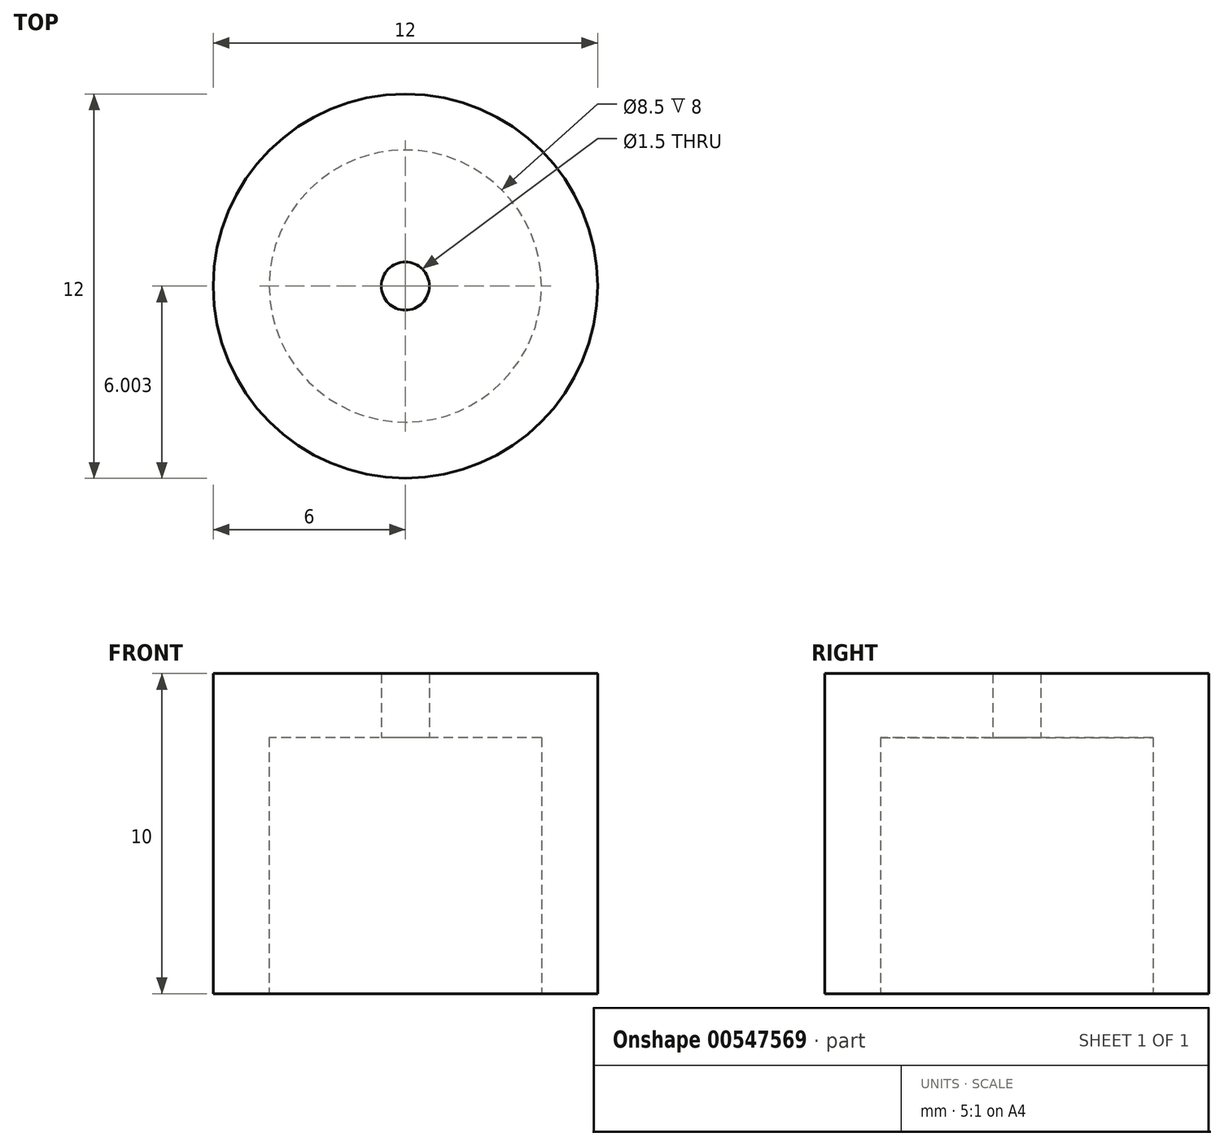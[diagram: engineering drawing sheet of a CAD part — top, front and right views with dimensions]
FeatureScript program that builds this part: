
annotation { "Feature Type Name" : "Feature", "Feature Type Description" : "" }
export const myFeature = defineFeature(function(context is Context, id is Id, definition is map)
    precondition{}
    {
        {
            var Q0;
            Q0=qCreatedBy(makeId("Top.planeOp"),FACE);
            var sketch = newSketch(context, id + "F0", { "sketchPlane" : qUnion([Q0])});
            skCircle(sketch, "E0", {"center": v(0, -0.55) * mm, "radius": 6 * mm});
            skCircle(sketch, "E1", {"center": v(0, -0.55) * mm, "radius": 4.25 * mm});
            skSolve(sketch);
        }
        {
            var Q0;
            Q0=makeQuery(id+"F0.imprint","IMPRINT",FACE,{"disambiguationData":[TD([[makeQuery(id+"F0.imprint","IMPRINT",EDGE,{"derivedFrom":sQuery(id+"F0.wireOp",EDGE,"E0")}),1.0]])]});
            var Q1;
            Q1=makeQuery(id+"F0.imprint","IMPRINT",FACE,{"disambiguationData":[TD([[makeQuery(id+"F0.imprint","IMPRINT",EDGE,{"derivedFrom":sQuery(id+"F0.wireOp",EDGE,"E1")}),1.0]])]});
            extrude(context, id + "F1", {"entities" : qUnion([Q0, Q1]), "depth" : 10 * mm});
        }
        {
            var Q0;
            Q0=makeQuery(id+"F0.imprint","IMPRINT",FACE,{"disambiguationData":[TD([[makeQuery(id+"F0.imprint","IMPRINT",EDGE,{"derivedFrom":sQuery(id+"F0.wireOp",EDGE,"E1")}),1.0]])]});
            extrude(context, id + "F2", {"entities" : qUnion([Q0]), "operationType" : NewBodyOperationType.REMOVE, "depth" : 8 * mm});
        }
        {
            var Q0;
            Q0=sQuery(id+"F0.wireOp",VERTEX,"E0.center");
            var Q1;
            Q1=makeQuery(id+"F1.opExtrude","SWEPT_BODY",BODY,{"disambiguationData":[OSD([sQuery(id+"F0.wireOp",EDGE,"E0")])]});
            hole(context, id + "F3", {"style" : HoleStyle.SIMPLE, "endStyle" : HoleEndStyle.THROUGH, "oppositeDirection" : true, "holeDiameter" : 1.5 * mm, "isTappedThrough" : true, "tappedDepth" : 12 * mm, "tapClearance" : 3, "locations" : qUnion([Q0]), "scope" : qUnion([Q1])});
        }
    });
